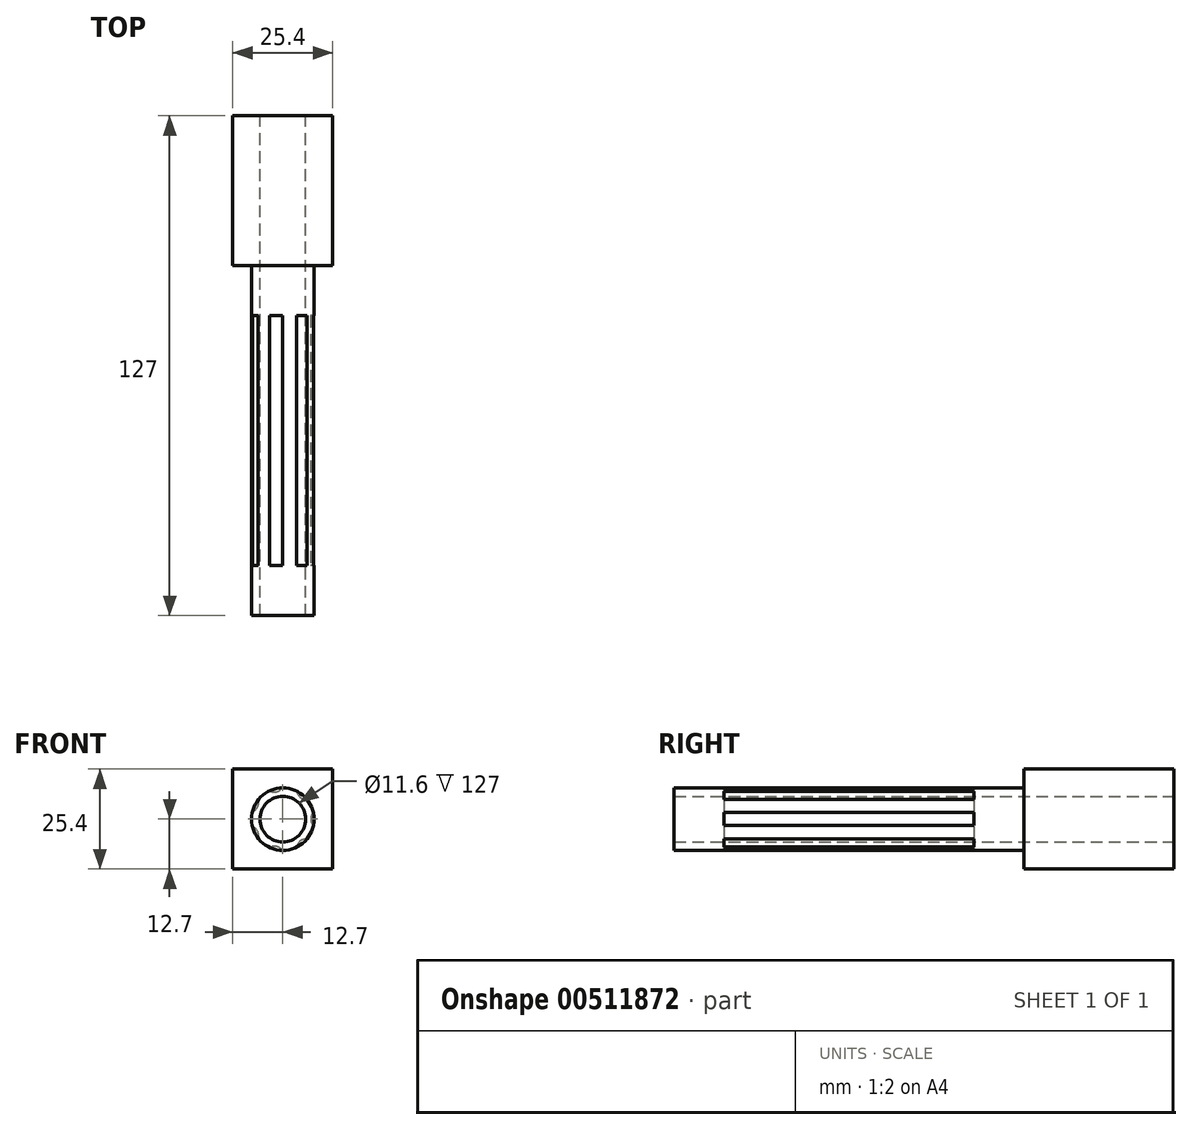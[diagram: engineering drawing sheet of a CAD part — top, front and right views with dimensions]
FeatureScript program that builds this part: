
annotation { "Feature Type Name" : "Feature", "Feature Type Description" : "" }
export const myFeature = defineFeature(function(context is Context, id is Id, definition is map)
    precondition{}
    {
        {
            var Q0;
            Q0=qCreatedBy(makeId("Front.planeOp"),FACE);
            var sketch = newSketch(context, id + "F0", { "sketchPlane" : qUnion([Q0])});
            skLineSegment(sketch, "E0.bottom", {"start": v(12.7, -12.7) * mm, "end": v(-12.7, -12.7) * mm});
            skLineSegment(sketch, "E0.top", {"start": v(12.7, 12.7) * mm, "end": v(-12.7, 12.7) * mm});
            skLineSegment(sketch, "E0.left", {"start": v(12.7, -12.7) * mm, "end": v(12.7, 12.7) * mm});
            skLineSegment(sketch, "E0.right", {"start": v(-12.7, -12.7) * mm, "end": v(-12.7, 12.7) * mm});
            skPoint(sketch, "E0.middle", {"position": v(0, 0) * mm});
            skCircle(sketch, "E1", {"center": v(0, 0) * mm, "radius": 7.94 * mm});
            skCircle(sketch, "E2", {"center": v(0, 0) * mm, "radius": 5.8 * mm});
            skSolve(sketch);
        }
        {
            var Q0;
            Q0=qSketchRegion(id+"F0",true);
            var Q1;
            Q1=makeQuery(id+"F0.imprint","IMPRINT",FACE,{"disambiguationData":[TD([[makeQuery(id+"F0.imprint","IMPRINT",EDGE,{"derivedFrom":sQuery(id+"F0.wireOp",EDGE,"E1")}),1.0]])]});
            extrude(context, id + "F1", {"entities" : qUnion([Q0, Q1]), "depth" : 38.1 * mm});
        }
        {
            var Q0;
            Q0=makeQuery(id+"F0.imprint","IMPRINT",FACE,{"disambiguationData":[TD([[makeQuery(id+"F0.imprint","IMPRINT",EDGE,{"derivedFrom":sQuery(id+"F0.wireOp",EDGE,"E1")}),1.0]])]});
            extrude(context, id + "F2", {"entities" : qUnion([Q0]), "operationType" : NewBodyOperationType.ADD, "depth" : 127 * mm, "offsetDistance" : 25.4 * mm});
        }
        {
            var Q0;
            Q0=makeQuery(id+"F2.opExtrude","CAP_FACE",FACE,{"disambiguationData":[OSD([sQuery(id+"F0.wireOp",EDGE,"E1")])],"isStart":false});
            var sketch = newSketch(context, id + "F3", { "sketchPlane" : qUnion([Q0])});
            skCircle(sketch, "E3", {"center": v(9.58, 0) * mm, "radius": 2.46 * mm});
            skCircle(sketch, "E4.1.0", {"center": v(5.97, 7.49) * mm, "radius": 2.46 * mm});
            skCircle(sketch, "E4.2.0", {"center": v(-2.13, 9.34) * mm, "radius": 2.46 * mm});
            skCircle(sketch, "E4.3.0", {"center": v(-8.63, 4.16) * mm, "radius": 2.46 * mm});
            skCircle(sketch, "E4.4.0", {"center": v(-8.63, -4.16) * mm, "radius": 2.46 * mm});
            skCircle(sketch, "E4.5.0", {"center": v(-2.13, -9.34) * mm, "radius": 2.46 * mm});
            skCircle(sketch, "E4.6.0", {"center": v(5.97, -7.49) * mm, "radius": 2.46 * mm});
            skPoint(sketch, "E4.center", {"position": v(0, 0) * mm});
            skSolve(sketch);
        }
        {
            var Q0;
            Q0=qSketchRegion(id+"F3",true);
            extrude(context, id + "F4", {"entities" : qUnion([Q0]), "operationType" : NewBodyOperationType.REMOVE, "oppositeDirection" : true, "depth" : 76.2 * mm, "offsetDistance" : 25.4 * mm, "hasSecondDirection" : true, "secondDirectionOppositeDirection" : true, "secondDirectionDepth" : 12.7 * mm});
        }
    });
